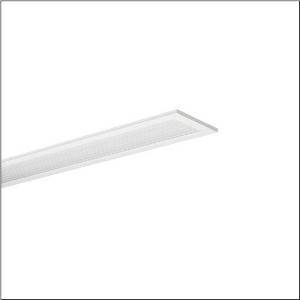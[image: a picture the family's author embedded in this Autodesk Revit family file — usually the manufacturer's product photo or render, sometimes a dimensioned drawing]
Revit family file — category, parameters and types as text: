
# Revit family: apollon_21_linear_51mq16wd2414
name_source: partatom
category: Lighting Fixtures
units: mm (PartAtom-declared; Revit-internal decimal feet)

## family parameters
Cut with Voids When Loaded = No
Host = Face
Light Source = No
Part Type = Normal
Room Calculation Point = No
Round Connector Dimension = Use Diameter
Shared = No

## types (1)
- Apollon 21 linear (1 x LED, 3400 lm, 23.2 W, 4000K)
    Apparent Load = 23 VA
    CIE Flux Codes = 64 88 97 100 100
    Color Rendering = 80
    Color Temperature = 4000K
    Default Elevation = 1800 mm
    Description = Apollon 21 linear, office luminaire, primary optical cover: micro prismatic cover, of PMMA, CAT 2 (L<= 3000cd/m²), light emission: direct distribution, primary light characteristic: symmetric, installation type: lay-in mounting, recessed, LED, rated luminous flux: 3.400lm, luminous efficacy: 147lm/W, light colour: 840, colour temperature: 4000K, control gear: DALI 2, Multilumen, with terminal, 5-pole, mains connection: 220..240V, AC/DC, 0/50..60Hz, rated input power: 23.2W, suitable for self-contained emergency lighting element 59MQE002602A with integrated self-test function according to EN 60598-2-22, housing, of aluminium, coated, traffic white (RAL 9016), module: M625, length: 1.545mm, width: 179mm, height: 55mm, housing upper side, of sheet steel, galvanised, protection rating (complete): IP20, protection rating (lamp compartment, on room side): IP50, insulation class (complete): insulation class II (safety insulation), certification: CE, ENEC, UKCA, impact resistance: IK03, permissible operating ambient temperature: -20..+45°C, standard: EN 60598-2-22, corresponds to IFS (International Featured Standards) requirements for safety and quality in the food industry, packaging unit: 1 piece
    Height = 0 mm  [stored 0 ft]
    Lamp = 1 x LED
    Lamp Light Flux = 3400 lm
    Lamp Power = 23.2 W
    Lamp count = 1
    Length = 1545 mm
    Luminous efficacy = 147 lm/W
    Manufacturer = Siteco
    ModVariant = No
    Model = 51MQ16WD2414
    Mounting Place = Ceiling
    Mounting Type = Recessed
    Number of Poles = 1
    OnlyDefault = Yes
    Power Factor = 1
    Product Name = Apollon 21 linear
    Product group = office luminaire | ceiling recessed
    ProductGroupID = 400
    Protection Class = Protection class II
    Protection Degree = IP 20
    RLX_Detail_Level = 1
    RLX_Emergency_Light_Flux = 0 lm
    RLX_Emergency_Type = 0
    RLX_Emergency_Type_DB = No
    RlxData = <blob elided: 12921 chars, md5=b9946be3>
    Socket = socket
    Standby Power = 0 W
    System Light Flux = 3400 lm
    System Power = 23 W
    Type Comments = Product without accessories
    Type Image = l_1291018.jpg
    URL = http://relux.com
    VarID = ---
    Voltage = 0 V
    Weight = 0.00 kg
    Width = 179 mm

note: [stored X ft] marks values corroborated as IEEE doubles in the binary element streams (Revit-internal decimal feet)

## geometry (parser evidence)
native form markers: Sweep x10
no freeform markers — native parametric forms only
